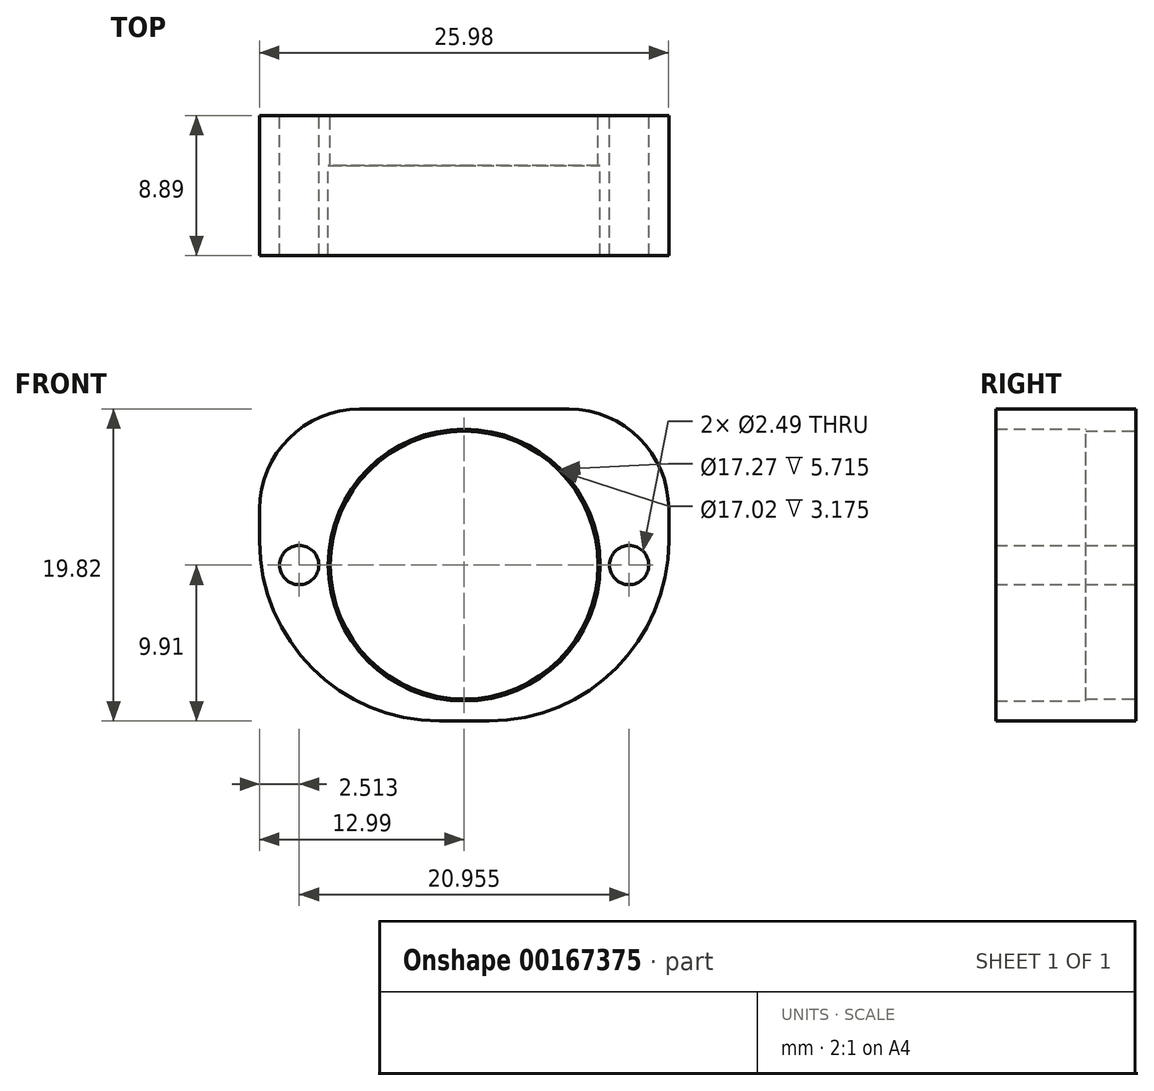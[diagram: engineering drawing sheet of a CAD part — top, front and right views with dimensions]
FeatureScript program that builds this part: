
annotation { "Feature Type Name" : "Feature", "Feature Type Description" : "" }
export const myFeature = defineFeature(function(context is Context, id is Id, definition is map)
    precondition{}
    {
        {
            var Q0;
            Q0=qCreatedBy(makeId("Front.planeOp"),FACE);
            var sketch = newSketch(context, id + "F0", { "sketchPlane" : qUnion([Q0])});
            skPoint(sketch, "E0.middle", {"position": v(0, 0) * mm});
            skCircle(sketch, "E1", {"center": v(0, 0) * mm, "radius": 8.5 * mm});
            skCircle(sketch, "E2", {"center": v(-10.48, 0) * mm, "radius": 1.24 * mm});
            skCircle(sketch, "E3", {"center": v(10.48, 0) * mm, "radius": 1.24 * mm});
            skLineSegment(sketch, "E4.bottom", {"start": v(-6.64, 9.9) * mm, "end": v(6.64, 9.9) * mm});
            skLineSegment(sketch, "E4.top", {"start": v(-1.56, -9.9) * mm, "end": v(1.56, -9.9) * mm});
            skLineSegment(sketch, "E4.left", {"start": v(-13, 3.56) * mm, "end": v(-13, 1.52) * mm});
            skLineSegment(sketch, "E4.right", {"start": v(13, 3.56) * mm, "end": v(13, 1.52) * mm});
            skPoint(sketch, "E5.visualSharp", {"position": v(-13, 9.9) * mm});
            skArc(sketch, "E5.filletArc", {"start": v(-6.64, 9.9) * mm, "mid": v(-11.13, 8.05) * mm, "end": v(-13, 3.56) * mm});
            skPoint(sketch, "E6.visualSharp", {"position": v(13, 9.9) * mm});
            skArc(sketch, "E6.filletArc", {"start": v(13, 3.56) * mm, "mid": v(11.13, 8.05) * mm, "end": v(6.64, 9.9) * mm});
            skPoint(sketch, "E7.visualSharp", {"position": v(13, -9.9) * mm});
            skArc(sketch, "E7.filletArc", {"start": v(1.56, -9.9) * mm, "mid": v(9.64, -6.56) * mm, "end": v(13, 1.52) * mm});
            skPoint(sketch, "E8.visualSharp", {"position": v(-13, -9.9) * mm});
            skArc(sketch, "E8.filletArc", {"start": v(-13, 1.52) * mm, "mid": v(-9.64, -6.56) * mm, "end": v(-1.56, -9.9) * mm});
            skCircle(sketch, "E9", {"center": v(0, 0) * mm, "radius": 8.64 * mm});
            skSolve(sketch);
        }
        {
            var Q0;
            Q0=makeQuery(id+"F0.imprint","IMPRINT",FACE,{"disambiguationData":[TD([[makeQuery(id+"F0.imprint","IMPRINT",EDGE,{"derivedFrom":sQuery(id+"F0.wireOp",EDGE,"E2")}),-1.0]])]});
            extrude(context, id + "F1", {"entities" : qUnion([Q0]), "depth" : 8.9 * mm});
        }
        {
            var Q0;
            Q0=makeQuery(id+"F0.imprint","IMPRINT",FACE,{"disambiguationData":[TD([[makeQuery(id+"F0.imprint","IMPRINT",EDGE,{"derivedFrom":sQuery(id+"F0.wireOp",EDGE,"E1")}),-1.0]])]});
            extrude(context, id + "F2", {"entities" : qUnion([Q0]), "operationType" : NewBodyOperationType.ADD, "depth" : 3.17 * mm});
        }
    });
